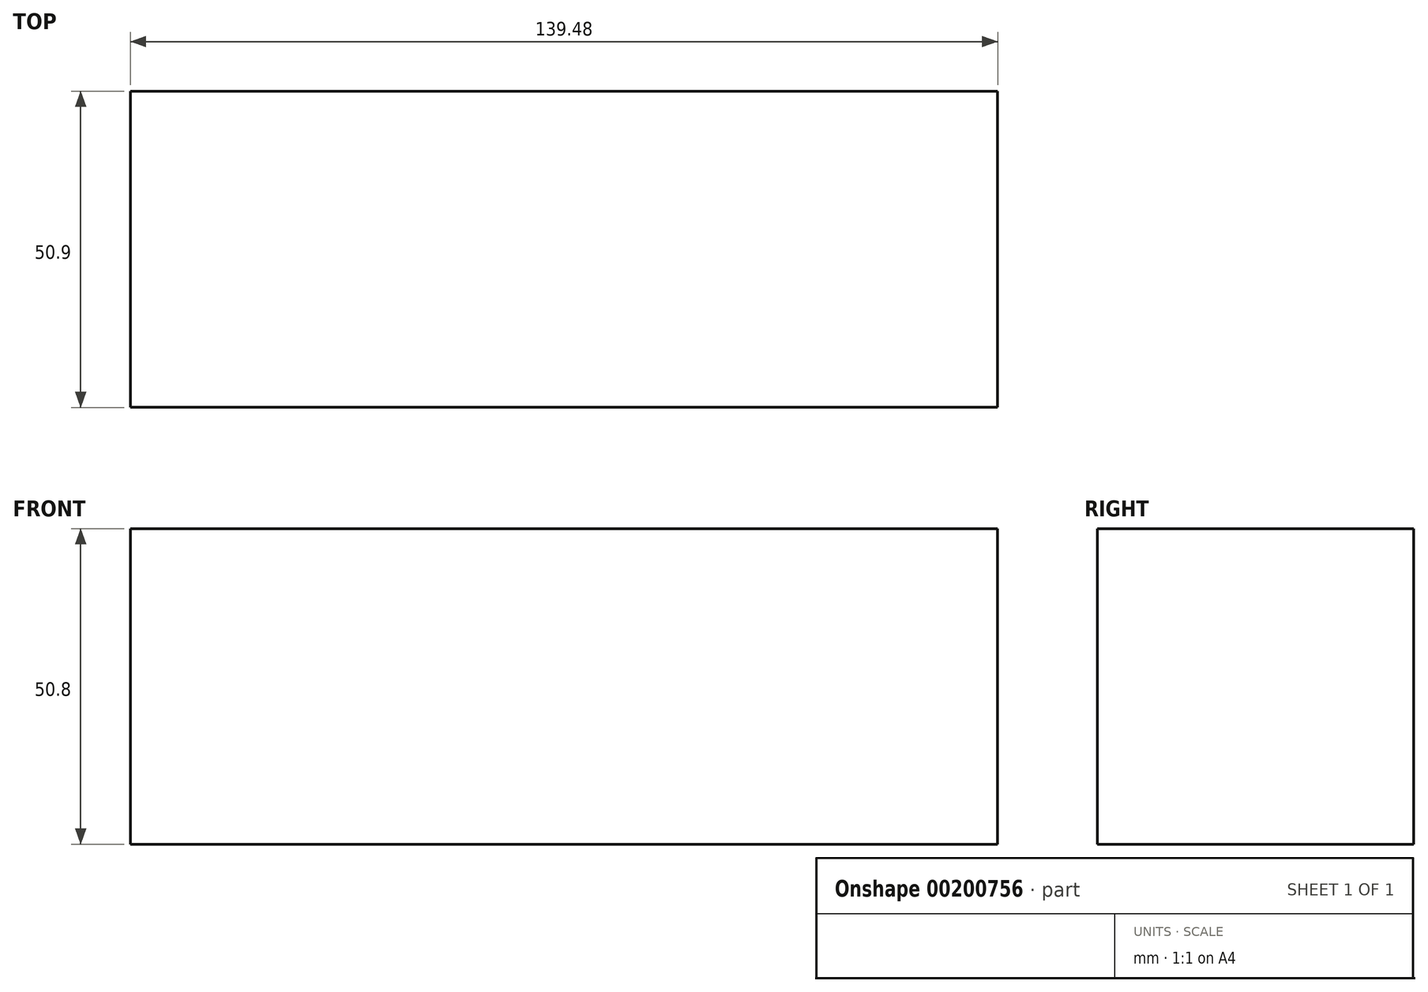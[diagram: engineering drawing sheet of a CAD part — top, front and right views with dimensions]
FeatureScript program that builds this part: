
annotation { "Feature Type Name" : "Feature", "Feature Type Description" : "" }
export const myFeature = defineFeature(function(context is Context, id is Id, definition is map)
    precondition{}
    {
        {
            var Q0;
            Q0=qCreatedBy(makeId("Top.planeOp"),FACE);
            var sketch = newSketch(context, id + "F0", { "sketchPlane" : qUnion([Q0])});
            skLineSegment(sketch, "E0.bottom", {"start": v(-62.55, 62.94) * mm, "end": v(76.93, 62.94) * mm});
            skLineSegment(sketch, "E0.top", {"start": v(-62.55, 12.04) * mm, "end": v(76.93, 12.04) * mm});
            skLineSegment(sketch, "E0.left", {"start": v(-62.55, 62.94) * mm, "end": v(-62.55, 12.04) * mm});
            skLineSegment(sketch, "E0.right", {"start": v(76.93, 62.94) * mm, "end": v(76.93, 12.04) * mm});
            skSolve(sketch);
        }
        {
            var Q0;
            Q0=makeQuery(id+"F0.imprint","IMPRINT",FACE,{"disambiguationData":[TD([[makeQuery(id+"F0.imprint","IMPRINT",EDGE,{"derivedFrom":sQuery(id+"F0.wireOp",EDGE,"E0.bottom")}),-1.0]])]});
            extrude(context, id + "F1", {"entities" : qUnion([Q0]), "depth" : 50.8 * mm});
        }
    });
